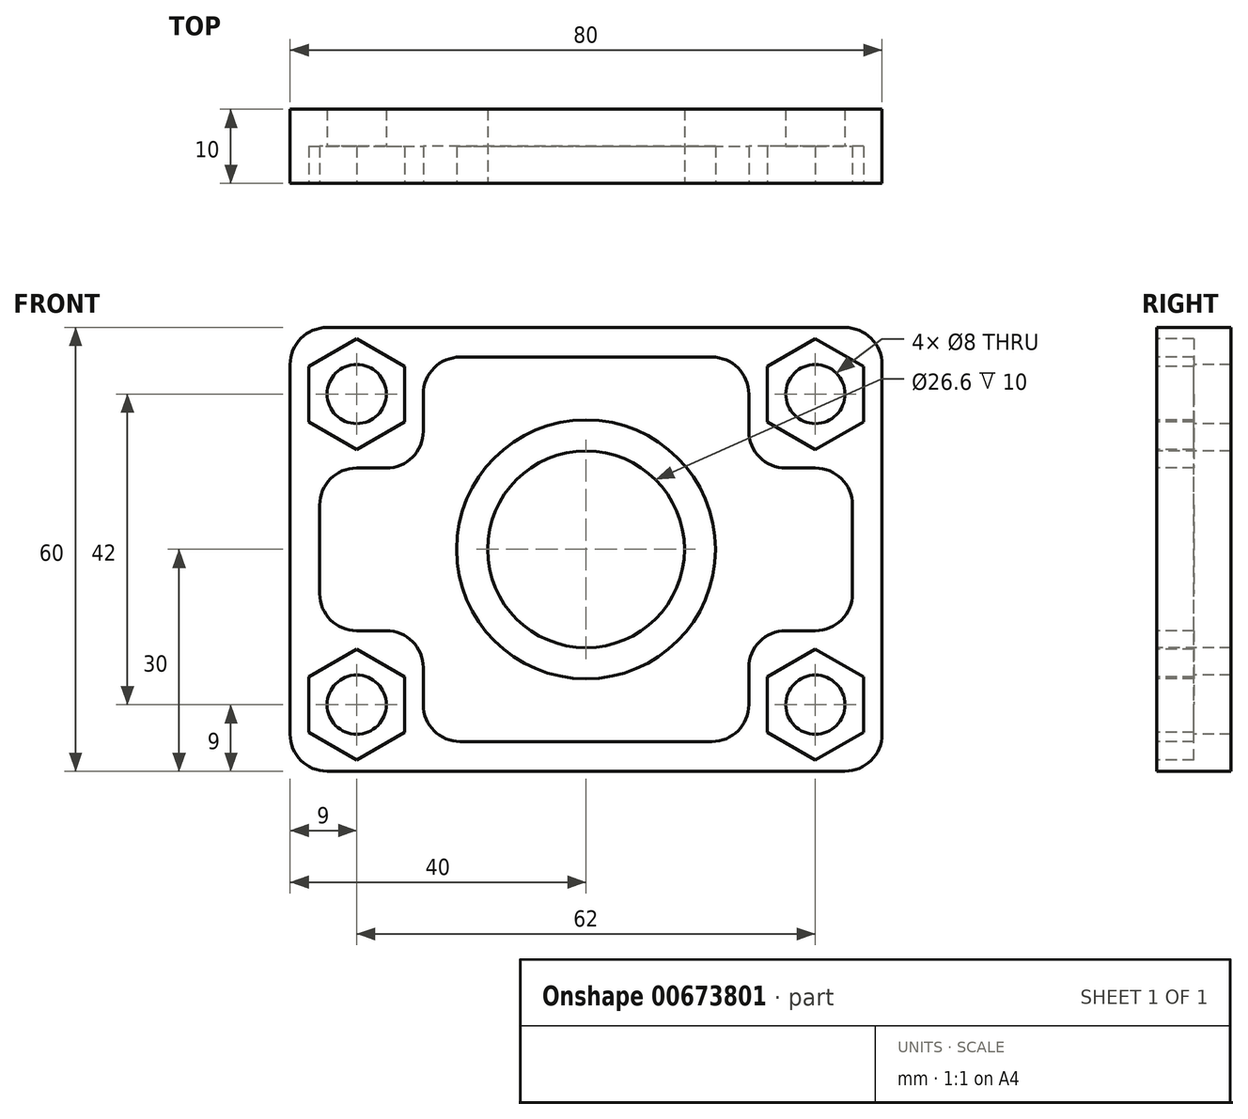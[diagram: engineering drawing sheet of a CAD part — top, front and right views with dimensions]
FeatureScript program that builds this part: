
annotation { "Feature Type Name" : "Feature", "Feature Type Description" : "" }
export const myFeature = defineFeature(function(context is Context, id is Id, definition is map)
    precondition{}
    {
        {
            var Q0;
            Q0=qCreatedBy(makeId("Front.planeOp"),FACE);
            var sketch = newSketch(context, id + "F0", { "sketchPlane" : qUnion([Q0])});
            skLineSegment(sketch, "E0.bottom", {"start": v(-40, 40) * mm, "end": v(40, 40) * mm});
            skLineSegment(sketch, "E0.top", {"start": v(-40, -20) * mm, "end": v(40, -20) * mm});
            skLineSegment(sketch, "E0.left", {"start": v(-40, 40) * mm, "end": v(-40, -20) * mm});
            skLineSegment(sketch, "E0.right", {"start": v(40, 40) * mm, "end": v(40, -20) * mm});
            skSolve(sketch);
        }
        {
            var Q0;
            Q0=qSketchRegion(id+"F0",true);
            extrude(context, id + "F1", {"entities" : qUnion([Q0]), "depth" : 10 * mm, "offsetDistance" : 25 * mm});
        }
        {
            var Q0;
            Q0=makeQuery(id+"F1.opExtrude","CAP_FACE",FACE,{"disambiguationData":[OSD([sQuery(id+"F0.wireOp",EDGE,"E0.bottom"),sQuery(id+"F0.wireOp",EDGE,"E0.top"),sQuery(id+"F0.wireOp",EDGE,"E0.left"),sQuery(id+"F0.wireOp",EDGE,"E0.right")])],"isStart":false});
            var sketch = newSketch(context, id + "F2", { "sketchPlane" : qUnion([Q0])});
            skCircle(sketch, "E1", {"center": v(0, 10) * mm, "radius": 13.3 * mm});
            skSolve(sketch);
        }
        {
            var Q0;
            Q0=qSketchRegion(id+"F2",true);
            extrude(context, id + "F3", {"entities" : qUnion([Q0]), "operationType" : NewBodyOperationType.REMOVE, "endBound" : BoundingType.THROUGH_ALL, "oppositeDirection" : true, "depth" : 25 * mm, "offsetDistance" : 25 * mm});
        }
        {
            var Q0;
            Q0=makeQuery(id+"F1.opExtrude","CAP_FACE",FACE,{"disambiguationData":[OSD([sQuery(id+"F0.wireOp",EDGE,"E0.bottom"),sQuery(id+"F0.wireOp",EDGE,"E0.top"),sQuery(id+"F0.wireOp",EDGE,"E0.left"),sQuery(id+"F0.wireOp",EDGE,"E0.right")])],"isStart":false});
            var sketch = newSketch(context, id + "F4", { "sketchPlane" : qUnion([Q0])});
            skCircle(sketch, "E2", {"center": v(-31, 31) * mm, "radius": 4 * mm});
            skCircle(sketch, "E3", {"center": v(31, 31) * mm, "radius": 4 * mm});
            skCircle(sketch, "E4", {"center": v(-31, -11) * mm, "radius": 4 * mm});
            skCircle(sketch, "E5", {"center": v(31, -11) * mm, "radius": 4 * mm});
            skSolve(sketch);
        }
        {
            var Q0;
            Q0=qSketchRegion(id+"F4",true);
            extrude(context, id + "F5", {"entities" : qUnion([Q0]), "operationType" : NewBodyOperationType.REMOVE, "endBound" : BoundingType.THROUGH_ALL, "oppositeDirection" : true, "depth" : 25 * mm, "offsetDistance" : 25 * mm});
        }
        {
            var Q0;
            Q0=makeQuery(id+"F1.opExtrude","SWEPT_EDGE",EDGE,{"disambiguationData":[OSD([sQuery(id+"F0.wireOp",EDGE,"E0.bottom"),sQuery(id+"F0.wireOp",EDGE,"E0.right")])]});
            var Q1;
            Q1=makeQuery(id+"F1.opExtrude","SWEPT_EDGE",EDGE,{"disambiguationData":[OSD([sQuery(id+"F0.wireOp",EDGE,"E0.top"),sQuery(id+"F0.wireOp",EDGE,"E0.right")])]});
            var Q2;
            Q2=makeQuery(id+"F1.opExtrude","SWEPT_EDGE",EDGE,{"disambiguationData":[OSD([sQuery(id+"F0.wireOp",EDGE,"E0.top"),sQuery(id+"F0.wireOp",EDGE,"E0.left")])]});
            var Q3;
            Q3=makeQuery(id+"F1.opExtrude","SWEPT_EDGE",EDGE,{"disambiguationData":[OSD([sQuery(id+"F0.wireOp",EDGE,"E0.bottom"),sQuery(id+"F0.wireOp",EDGE,"E0.left")])]});
            fillet(context, id + "F6", {"entities" : qUnion([Q0, Q1, Q2, Q3]), "radius" : 5 * mm, "tangentPropagation" : true, "allowEdgeOverflow" : false});
        }
        {
            var Q0;
            Q0=makeQuery(id+"F4.imprint","IMPRINT",FACE,{"disambiguationData":[TD([[makeQuery(id+"F4.imprint","IMPRINT",EDGE,{"derivedFrom":sQuery(id+"F4.wireOp",EDGE,"E2")}),-1.0]])]});
            var sketch = newSketch(context, id + "F7", { "sketchPlane" : qUnion([Q0])});
            skCircle(sketch, "E6.cCircle", {"center": v(-31, 31) * mm, "radius": 6.5 * mm, "construction": true});
            skLineSegment(sketch, "E6.0", {"start": v(-31, 38.5) * mm, "end": v(-24.5, 34.75) * mm});
            skLineSegment(sketch, "E6.1", {"start": v(-24.5, 34.75) * mm, "end": v(-24.5, 27.25) * mm});
            skLineSegment(sketch, "E6.2", {"start": v(-24.5, 27.25) * mm, "end": v(-31, 23.5) * mm});
            skLineSegment(sketch, "E6.3", {"start": v(-31, 23.5) * mm, "end": v(-37.5, 27.25) * mm});
            skLineSegment(sketch, "E6.4", {"start": v(-37.5, 27.25) * mm, "end": v(-37.5, 34.75) * mm});
            skLineSegment(sketch, "E6.5", {"start": v(-37.5, 34.75) * mm, "end": v(-31, 38.5) * mm});
            skPoint(sketch, "E6.0.midPoint", {"position": v(-27.75, 36.63) * mm});
            skCircle(sketch, "E7.cCircle", {"center": v(31, 31) * mm, "radius": 6.5 * mm, "construction": true});
            skLineSegment(sketch, "E7.0", {"start": v(24.5, 27.25) * mm, "end": v(24.5, 34.75) * mm});
            skLineSegment(sketch, "E7.1", {"start": v(24.5, 34.75) * mm, "end": v(31, 38.5) * mm});
            skLineSegment(sketch, "E7.2", {"start": v(31, 38.5) * mm, "end": v(37.5, 34.75) * mm});
            skLineSegment(sketch, "E7.3", {"start": v(37.5, 34.75) * mm, "end": v(37.5, 27.25) * mm});
            skLineSegment(sketch, "E7.4", {"start": v(37.5, 27.25) * mm, "end": v(31, 23.5) * mm});
            skLineSegment(sketch, "E7.5", {"start": v(31, 23.5) * mm, "end": v(24.5, 27.25) * mm});
            skPoint(sketch, "E7.0.midPoint", {"position": v(24.5, 31) * mm});
            skCircle(sketch, "E8.cCircle", {"center": v(31, -11) * mm, "radius": 6.5 * mm, "construction": true});
            skLineSegment(sketch, "E8.0", {"start": v(24.5, -14.75) * mm, "end": v(24.5, -7.25) * mm});
            skLineSegment(sketch, "E8.1", {"start": v(24.5, -7.25) * mm, "end": v(31, -3.5) * mm});
            skLineSegment(sketch, "E8.2", {"start": v(31, -3.5) * mm, "end": v(37.5, -7.25) * mm});
            skLineSegment(sketch, "E8.3", {"start": v(37.5, -7.25) * mm, "end": v(37.5, -14.75) * mm});
            skLineSegment(sketch, "E8.4", {"start": v(37.5, -14.75) * mm, "end": v(31, -18.5) * mm});
            skLineSegment(sketch, "E8.5", {"start": v(31, -18.5) * mm, "end": v(24.5, -14.75) * mm});
            skPoint(sketch, "E8.0.midPoint", {"position": v(24.5, -11) * mm});
            skCircle(sketch, "E9.cCircle", {"center": v(-31, -11) * mm, "radius": 6.5 * mm, "construction": true});
            skLineSegment(sketch, "E9.0", {"start": v(-31, -3.5) * mm, "end": v(-24.5, -7.25) * mm});
            skLineSegment(sketch, "E9.1", {"start": v(-24.5, -7.25) * mm, "end": v(-24.5, -14.75) * mm});
            skLineSegment(sketch, "E9.2", {"start": v(-24.5, -14.75) * mm, "end": v(-31, -18.5) * mm});
            skLineSegment(sketch, "E9.3", {"start": v(-31, -18.5) * mm, "end": v(-37.5, -14.75) * mm});
            skLineSegment(sketch, "E9.4", {"start": v(-37.5, -14.75) * mm, "end": v(-37.5, -7.25) * mm});
            skLineSegment(sketch, "E9.5", {"start": v(-37.5, -7.25) * mm, "end": v(-31, -3.5) * mm});
            skPoint(sketch, "E9.0.midPoint", {"position": v(-27.75, -5.37) * mm});
            skCircle(sketch, "E10", {"center": v(0, 10) * mm, "radius": 17.5 * mm});
            skLineSegment(sketch, "E11.bottom", {"start": v(-22, 36) * mm, "end": v(22, 36) * mm});
            skLineSegment(sketch, "E11.top", {"start": v(-22, -16) * mm, "end": v(22, -16) * mm});
            skLineSegment(sketch, "E11.left", {"start": v(-22, 36) * mm, "end": v(-22, -16) * mm});
            skLineSegment(sketch, "E11.right", {"start": v(22, 36) * mm, "end": v(22, -16) * mm});
            skLineSegment(sketch, "E12.bottom", {"start": v(36, 21) * mm, "end": v(-36, 21) * mm});
            skLineSegment(sketch, "E12.top", {"start": v(36, -1) * mm, "end": v(-36, -1) * mm});
            skLineSegment(sketch, "E12.left", {"start": v(36, 21) * mm, "end": v(36, -1) * mm});
            skLineSegment(sketch, "E12.right", {"start": v(-36, 21) * mm, "end": v(-36, -1) * mm});
            skSolve(sketch);
        }
        {
            var Q0;
            Q0 = qSketchRegion(id + "F7", true);
            extrude(context, id + "F8", {"entities" : qUnion([Q0]), "operationType" : NewBodyOperationType.REMOVE, "oppositeDirection" : true, "depth" : 5 * mm, "offsetDistance" : 25 * mm});
        }
        {
            var Q0;
            Q0=makeQuery(id+"F8.boolean.opBoolean","COPY",EDGE,{"derivedFrom":makeQuery(id+"F8.opExtrude","SWEPT_EDGE",EDGE,{"disambiguationData":[OSD([sQuery(id+"F7.wireOp",EDGE,"E11.left"),sQuery(id+"F7.wireOp",EDGE,"E12.bottom")])]})});
            var Q1;
            Q1=makeQuery(id+"F8.boolean.opBoolean","COPY",EDGE,{"derivedFrom":makeQuery(id+"F8.opExtrude","SWEPT_EDGE",EDGE,{"disambiguationData":[OSD([sQuery(id+"F7.wireOp",EDGE,"E12.bottom"),sQuery(id+"F7.wireOp",EDGE,"E12.right")])]})});
            var Q2;
            Q2=makeQuery(id+"F8.boolean.opBoolean","COPY",EDGE,{"derivedFrom":makeQuery(id+"F8.opExtrude","SWEPT_EDGE",EDGE,{"disambiguationData":[OSD([sQuery(id+"F7.wireOp",EDGE,"E11.bottom"),sQuery(id+"F7.wireOp",EDGE,"E11.left")])]})});
            var Q3;
            Q3=makeQuery(id+"F8.boolean.opBoolean","COPY",EDGE,{"derivedFrom":makeQuery(id+"F8.opExtrude","SWEPT_EDGE",EDGE,{"disambiguationData":[OSD([sQuery(id+"F7.wireOp",EDGE,"E11.bottom"),sQuery(id+"F7.wireOp",EDGE,"E11.right")])]})});
            var Q4;
            Q4=makeQuery(id+"F8.boolean.opBoolean","COPY",EDGE,{"derivedFrom":makeQuery(id+"F8.opExtrude","SWEPT_EDGE",EDGE,{"disambiguationData":[OSD([sQuery(id+"F7.wireOp",EDGE,"E11.right"),sQuery(id+"F7.wireOp",EDGE,"E12.bottom")])]})});
            var Q5;
            Q5=makeQuery(id+"F8.boolean.opBoolean","COPY",EDGE,{"derivedFrom":makeQuery(id+"F8.opExtrude","SWEPT_EDGE",EDGE,{"disambiguationData":[OSD([sQuery(id+"F7.wireOp",EDGE,"E12.bottom"),sQuery(id+"F7.wireOp",EDGE,"E12.left")])]})});
            var Q6;
            Q6=makeQuery(id+"F8.boolean.opBoolean","COPY",EDGE,{"derivedFrom":makeQuery(id+"F8.opExtrude","SWEPT_EDGE",EDGE,{"disambiguationData":[OSD([sQuery(id+"F7.wireOp",EDGE,"E12.top"),sQuery(id+"F7.wireOp",EDGE,"E12.right")])]})});
            var Q7;
            Q7=makeQuery(id+"F8.boolean.opBoolean","COPY",EDGE,{"derivedFrom":makeQuery(id+"F8.opExtrude","SWEPT_EDGE",EDGE,{"disambiguationData":[OSD([sQuery(id+"F7.wireOp",EDGE,"E11.left"),sQuery(id+"F7.wireOp",EDGE,"E12.top")])]})});
            var Q8;
            Q8=makeQuery(id+"F8.boolean.opBoolean","COPY",EDGE,{"derivedFrom":makeQuery(id+"F8.opExtrude","SWEPT_EDGE",EDGE,{"disambiguationData":[OSD([sQuery(id+"F7.wireOp",EDGE,"E11.top"),sQuery(id+"F7.wireOp",EDGE,"E11.left")])]})});
            var Q9;
            Q9=makeQuery(id+"F8.boolean.opBoolean","COPY",EDGE,{"derivedFrom":makeQuery(id+"F8.opExtrude","SWEPT_EDGE",EDGE,{"disambiguationData":[OSD([sQuery(id+"F7.wireOp",EDGE,"E12.top"),sQuery(id+"F7.wireOp",EDGE,"E12.left")])]})});
            var Q10;
            Q10=makeQuery(id+"F8.boolean.opBoolean","COPY",EDGE,{"derivedFrom":makeQuery(id+"F8.opExtrude","SWEPT_EDGE",EDGE,{"disambiguationData":[OSD([sQuery(id+"F7.wireOp",EDGE,"E11.right"),sQuery(id+"F7.wireOp",EDGE,"E12.top")])]})});
            var Q11;
            Q11=makeQuery(id+"F8.boolean.opBoolean","COPY",EDGE,{"derivedFrom":makeQuery(id+"F8.opExtrude","SWEPT_EDGE",EDGE,{"disambiguationData":[OSD([sQuery(id+"F7.wireOp",EDGE,"E11.top"),sQuery(id+"F7.wireOp",EDGE,"E11.right")])]})});
            fillet(context, id + "F9", {"entities" : qUnion([Q0, Q1, Q2, Q3, Q4, Q5, Q6, Q7, Q8, Q9, Q10, Q11]), "radius" : 5 * mm, "tangentPropagation" : true, "allowEdgeOverflow" : false});
        }
    });
